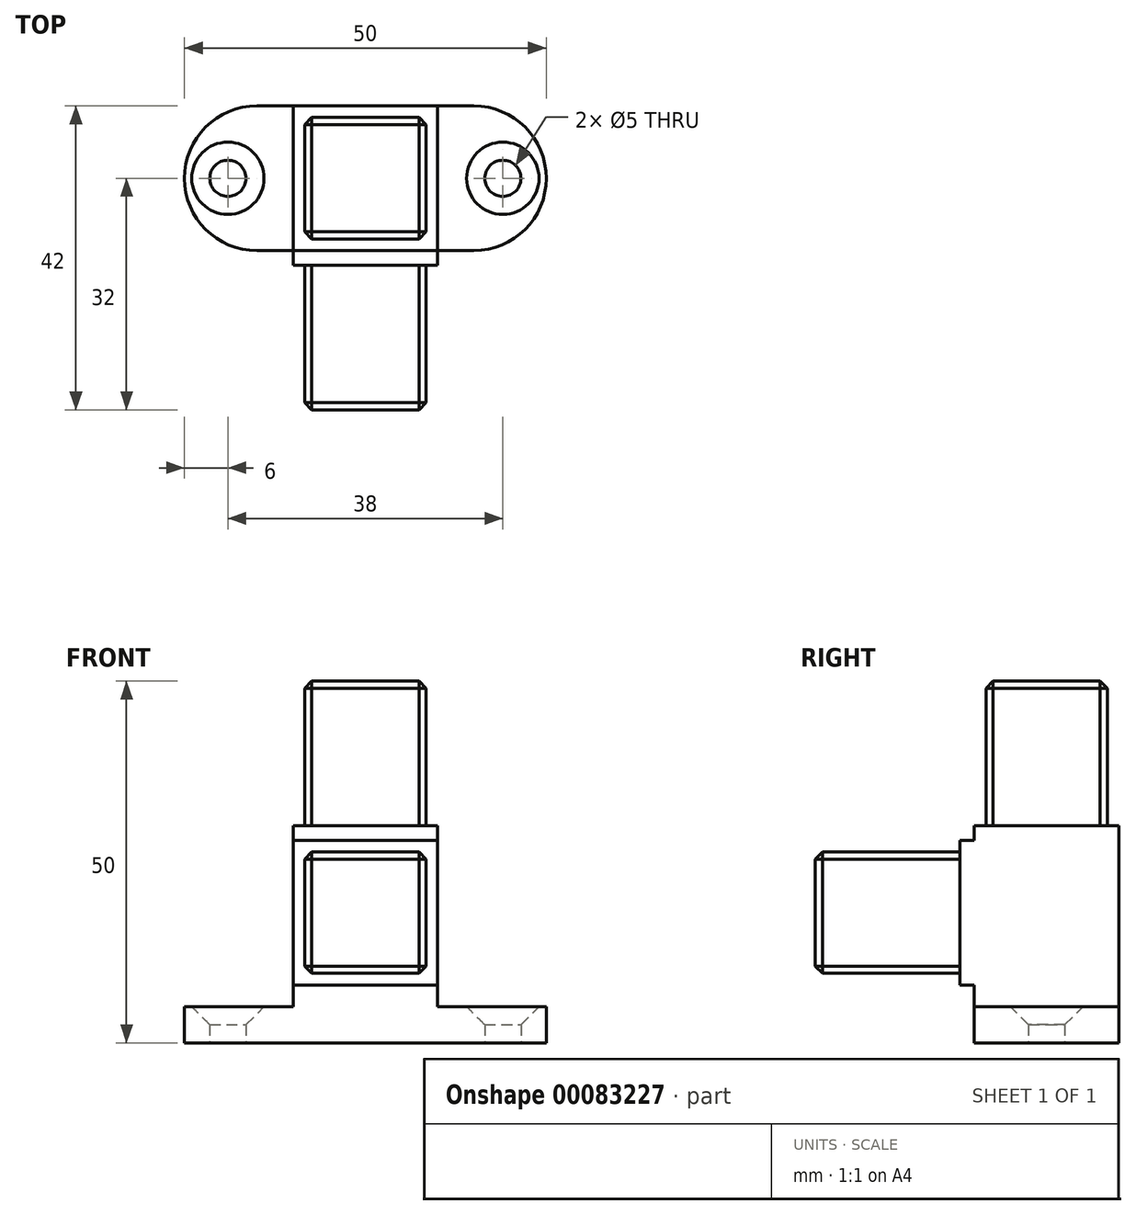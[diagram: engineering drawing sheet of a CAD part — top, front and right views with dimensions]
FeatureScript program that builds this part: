
annotation { "Feature Type Name" : "Feature", "Feature Type Description" : "" }
export const myFeature = defineFeature(function(context is Context, id is Id, definition is map)
    precondition{}
    {
        {
            var Q0;
            Q0=qCreatedBy(makeId("Top.planeOp"),FACE);
            var sketch = newSketch(context, id + "F0", { "sketchPlane" : qUnion([Q0])});
            skLineSegment(sketch, "E0.bottom", {"start": v(0, 0) * mm, "end": v(30, 0) * mm});
            skLineSegment(sketch, "E0.top", {"start": v(0, 20) * mm, "end": v(30, 20) * mm});
            skLineSegment(sketch, "E0.left", {"start": v(0, 0) * mm, "end": v(0, 20) * mm});
            skLineSegment(sketch, "E0.right", {"start": v(30, 0) * mm, "end": v(30, 20) * mm});
            skArc(sketch, "E1", {"start": v(0, 20) * mm, "mid": v(-10, 10) * mm, "end": v(0, 0) * mm});
            skArc(sketch, "E2", {"start": v(30, 0) * mm, "mid": v(40, 10) * mm, "end": v(30, 20) * mm});
            skLineSegment(sketch, "E3", {"start": v(5, 20) * mm, "end": v(5, 0) * mm});
            skLineSegment(sketch, "E4", {"start": v(25, 20) * mm, "end": v(25, 0) * mm});
            skPoint(sketch, "E5", {"position": v(-4, 10) * mm});
            skPoint(sketch, "E6", {"position": v(34, 10) * mm});
            skSolve(sketch);
        }
        {
            var Q0;
            {var subQ1=sQuery(id+"F0.wireOp",EDGE,"E3");Q0=makeQuery(id+"F0.imprint","IMPRINT",FACE,{"disambiguationData":[TD([[makeQuery(id+"F0.imprint","IMPRINT",EDGE,{"derivedFrom":subQ1}),1.0]])]});}
            extrude(context, id + "F1", {"entities" : qUnion([Q0]), "depth" : 25 * mm});
        }
        {
            var Q0;
            Q0=qSketchRegion(id+"F0",true);
            extrude(context, id + "F2", {"entities" : qUnion([Q0]), "operationType" : NewBodyOperationType.ADD, "oppositeDirection" : true, "depth" : 5 * mm});
        }
        {
            var Q0;
            Q0=makeQuery(id+"F1.opExtrude","CAP_FACE",FACE,{"disambiguationData":[OSD([sQuery(id+"F0.wireOp",EDGE,"E0.bottom"),sQuery(id+"F0.wireOp",EDGE,"E0.top"),sQuery(id+"F0.wireOp",EDGE,"E3"),sQuery(id+"F0.wireOp",EDGE,"E4")])],"isStart":false});
            var sketch = newSketch(context, id + "F3", { "sketchPlane" : qUnion([Q0])});
            skLineSegment(sketch, "E7", {"start": v(6.6, 18.4) * mm, "end": v(23.4, 18.4) * mm});
            skLineSegment(sketch, "E8", {"start": v(23.4, 18.4) * mm, "end": v(23.4, 1.6) * mm});
            skLineSegment(sketch, "E9", {"start": v(6.6, 18.4) * mm, "end": v(6.6, 1.6) * mm});
            skLineSegment(sketch, "E10", {"start": v(6.6, 1.6) * mm, "end": v(23.4, 1.6) * mm});
            skSolve(sketch);
        }
        {
            var Q0;
            Q0=makeQuery(id+"F3.imprint","IMPRINT",FACE,{"disambiguationData":[TD([[makeQuery(id+"F3.imprint","IMPRINT",EDGE,{"derivedFrom":sQuery(id+"F3.wireOp",EDGE,"E7")}),-1.0]])]});
            extrude(context, id + "F4", {"entities" : qUnion([Q0]), "operationType" : NewBodyOperationType.ADD, "depth" : 20 * mm});
        }
        {
            var Q0;
            {var subQ0=sQuery(id+"F0.wireOp",EDGE,"E0.bottom");Q0=makeQuery(id+"F2.boolean.opBoolean","MERGE",FACE,{"derivedFrom":[makeQuery(id+"F1.opExtrude","SWEPT_FACE",FACE,{"disambiguationData":[OSD([subQ0])]}),makeQuery(id+"F2.opExtrude","SWEPT_FACE",FACE,{"disambiguationData":[OSD([subQ0])]})]});}
            var sketch = newSketch(context, id + "F5", { "sketchPlane" : qUnion([Q0])});
            skLineSegment(sketch, "E11", {"start": v(5, 23) * mm, "end": v(25, 23) * mm});
            skLineSegment(sketch, "E12", {"start": v(25, 23) * mm, "end": v(25, 3) * mm});
            skLineSegment(sketch, "E13", {"start": v(25, 3) * mm, "end": v(5, 3) * mm});
            skLineSegment(sketch, "E14", {"start": v(5, 3) * mm, "end": v(5, 23) * mm});
            skSolve(sketch);
        }
        {
            var Q0;
            Q0=makeQuery(id+"F5.imprint","IMPRINT",FACE,{"disambiguationData":[TD([[makeQuery(id+"F5.imprint","IMPRINT",EDGE,{"derivedFrom":sQuery(id+"F5.wireOp",EDGE,"E11")}),-1.0]])]});
            extrude(context, id + "F6", {"entities" : qUnion([Q0]), "operationType" : NewBodyOperationType.ADD, "depth" : 2 * mm});
        }
        {
            var Q0;
            Q0=makeQuery(id+"F4.opExtrude","SWEPT_EDGE",EDGE,{"disambiguationData":[OSD([sQuery(id+"F3.wireOp",EDGE,"E7"),sQuery(id+"F3.wireOp",EDGE,"E8")])]});
            var Q1;
            Q1=makeQuery(id+"F4.opExtrude","SWEPT_EDGE",EDGE,{"disambiguationData":[OSD([sQuery(id+"F3.wireOp",EDGE,"E7"),sQuery(id+"F3.wireOp",EDGE,"E9")])]});
            var Q2;
            Q2=makeQuery(id+"F4.opExtrude","CAP_EDGE",EDGE,{"disambiguationData":[OSD([sQuery(id+"F3.wireOp",EDGE,"E7")])],"isStart":false});
            var Q3;
            Q3=makeQuery(id+"F4.opExtrude","CAP_EDGE",EDGE,{"disambiguationData":[OSD([sQuery(id+"F3.wireOp",EDGE,"E9")])],"isStart":false});
            var Q4;
            Q4=makeQuery(id+"F4.opExtrude","CAP_EDGE",EDGE,{"disambiguationData":[OSD([sQuery(id+"F3.wireOp",EDGE,"E8")])],"isStart":false});
            var Q5;
            Q5=makeQuery(id+"F4.opExtrude","CAP_EDGE",EDGE,{"disambiguationData":[OSD([sQuery(id+"F3.wireOp",EDGE,"E10")])],"isStart":false});
            var Q6;
            Q6=makeQuery(id+"F4.opExtrude","SWEPT_EDGE",EDGE,{"disambiguationData":[OSD([sQuery(id+"F3.wireOp",EDGE,"E8"),sQuery(id+"F3.wireOp",EDGE,"E10")])]});
            var Q7;
            Q7=makeQuery(id+"F4.opExtrude","SWEPT_EDGE",EDGE,{"disambiguationData":[OSD([sQuery(id+"F3.wireOp",EDGE,"E9"),sQuery(id+"F3.wireOp",EDGE,"E10")])]});
            chamfer(context, id + "F7", {"entities" : qUnion([Q0, Q1, Q2, Q3, Q4, Q5, Q6, Q7]), "width" : 1 * mm, "tangentPropagation" : true});
        }
        {
            var Q0;
            Q0=makeQuery(id+"F6.opExtrude","CAP_FACE",FACE,{"disambiguationData":[OSD([sQuery(id+"F5.wireOp",EDGE,"E11"),sQuery(id+"F5.wireOp",EDGE,"E12"),sQuery(id+"F5.wireOp",EDGE,"E13"),sQuery(id+"F5.wireOp",EDGE,"E14")])],"isStart":false});
            var sketch = newSketch(context, id + "F8", { "sketchPlane" : qUnion([Q0])});
            skLineSegment(sketch, "E15", {"start": v(6.6, 21.4) * mm, "end": v(23.4, 21.4) * mm});
            skLineSegment(sketch, "E16", {"start": v(23.4, 21.4) * mm, "end": v(23.4, 4.6) * mm});
            skLineSegment(sketch, "E17", {"start": v(23.4, 4.6) * mm, "end": v(6.6, 4.6) * mm});
            skLineSegment(sketch, "E18", {"start": v(6.6, 4.6) * mm, "end": v(6.6, 21.4) * mm});
            skSolve(sketch);
        }
        {
            var Q0;
            Q0=makeQuery(id+"F8.imprint","IMPRINT",FACE,{"disambiguationData":[TD([[makeQuery(id+"F8.imprint","IMPRINT",EDGE,{"derivedFrom":sQuery(id+"F8.wireOp",EDGE,"E15")}),-1.0]])]});
            extrude(context, id + "F9", {"entities" : qUnion([Q0]), "operationType" : NewBodyOperationType.ADD, "depth" : 20 * mm});
        }
        {
            var Q0;
            Q0=makeQuery(id+"F9.opExtrude","SWEPT_EDGE",EDGE,{"disambiguationData":[OSD([sQuery(id+"F8.wireOp",EDGE,"E15"),sQuery(id+"F8.wireOp",EDGE,"E16")])]});
            var Q1;
            Q1=makeQuery(id+"F9.opExtrude","CAP_EDGE",EDGE,{"disambiguationData":[OSD([sQuery(id+"F8.wireOp",EDGE,"E15")])],"isStart":false});
            var Q2;
            Q2=makeQuery(id+"F9.opExtrude","SWEPT_EDGE",EDGE,{"disambiguationData":[OSD([sQuery(id+"F8.wireOp",EDGE,"E15"),sQuery(id+"F8.wireOp",EDGE,"E18")])]});
            var Q3;
            Q3=makeQuery(id+"F9.opExtrude","CAP_EDGE",EDGE,{"disambiguationData":[OSD([sQuery(id+"F8.wireOp",EDGE,"E16")])],"isStart":false});
            var Q4;
            Q4=makeQuery(id+"F9.opExtrude","SWEPT_EDGE",EDGE,{"disambiguationData":[OSD([sQuery(id+"F8.wireOp",EDGE,"E16"),sQuery(id+"F8.wireOp",EDGE,"E17")])]});
            var Q5;
            Q5=makeQuery(id+"F9.opExtrude","SWEPT_EDGE",EDGE,{"disambiguationData":[OSD([sQuery(id+"F8.wireOp",EDGE,"E17"),sQuery(id+"F8.wireOp",EDGE,"E18")])]});
            var Q6;
            Q6=makeQuery(id+"F9.opExtrude","CAP_EDGE",EDGE,{"disambiguationData":[OSD([sQuery(id+"F8.wireOp",EDGE,"E18")])],"isStart":false});
            var Q7;
            Q7=makeQuery(id+"F9.opExtrude","CAP_EDGE",EDGE,{"disambiguationData":[OSD([sQuery(id+"F8.wireOp",EDGE,"E17")])],"isStart":false});
            chamfer(context, id + "F10", {"entities" : qUnion([Q0, Q1, Q2, Q3, Q4, Q5, Q6, Q7]), "width" : 1 * mm, "tangentPropagation" : true});
        }
        {
            var Q0;
            Q0=sQuery(id+"F0.wireOp",VERTEX,"E5");
            var Q1;
            Q1=sQuery(id+"F0.wireOp",VERTEX,"E6");
            var Q2;
            Q2=makeQuery(id+"F1.opExtrude","SWEPT_BODY",BODY,{"disambiguationData":[OSD([sQuery(id+"F0.wireOp",EDGE,"E0.bottom"),sQuery(id+"F0.wireOp",EDGE,"E0.top"),sQuery(id+"F0.wireOp",EDGE,"E3"),sQuery(id+"F0.wireOp",EDGE,"E4")])]});
            hole(context, id + "F11", {"style" : HoleStyle.C_SINK, "endStyle" : HoleEndStyle.THROUGH, "holeDiameter" : 5 * mm, "cSinkDiameter" : 10 * mm, "cSinkAngle" : 90 * degree, "locations" : qUnion([Q0, Q1]), "scope" : qUnion([Q2]), "isTappedThrough" : true, "startStyle" : HoleStartStyle.PART});
        }
    });
